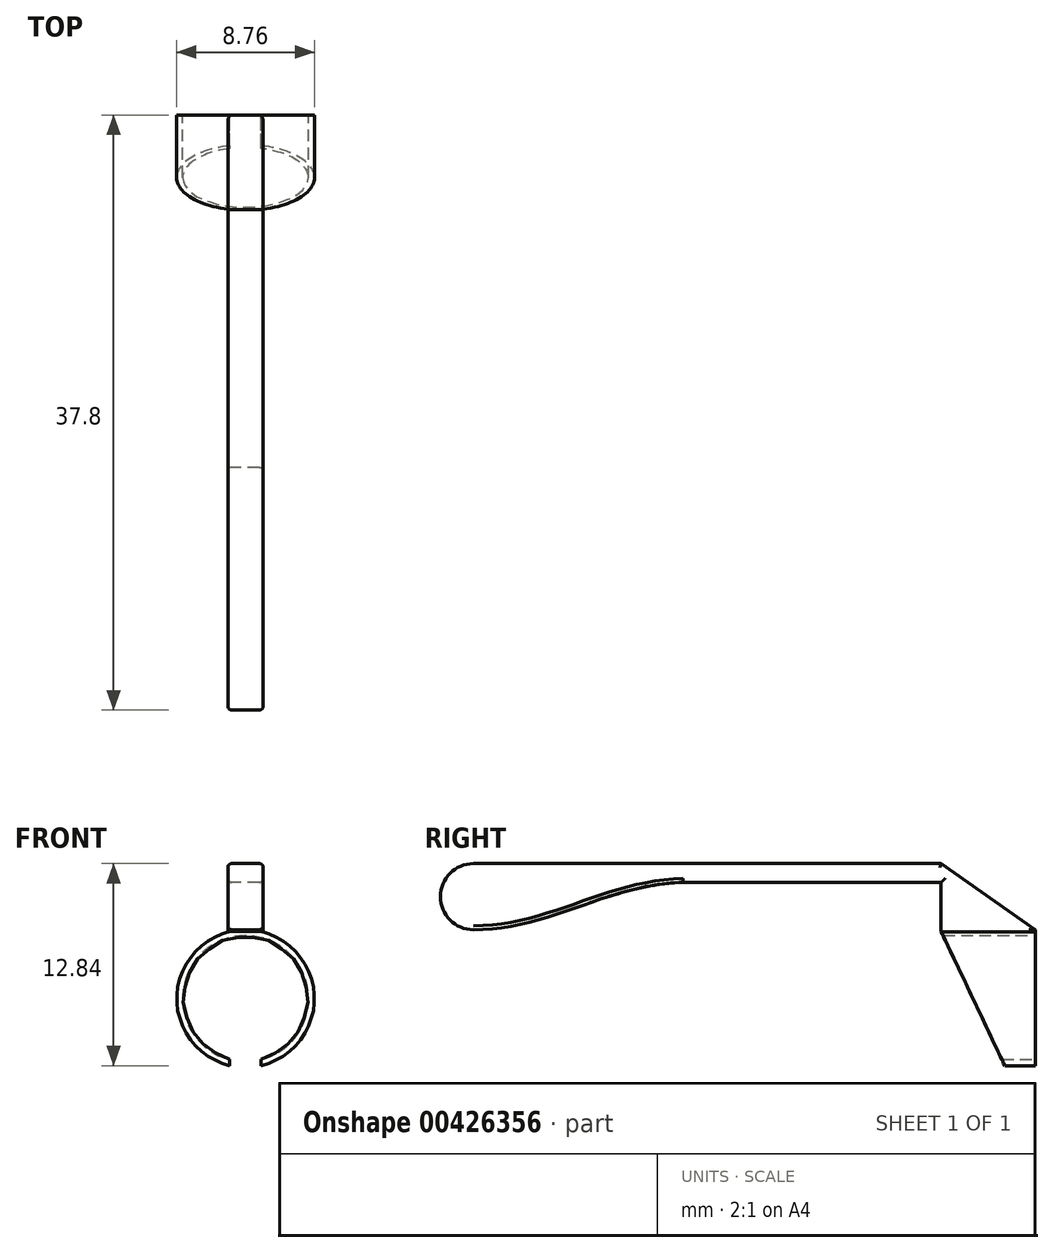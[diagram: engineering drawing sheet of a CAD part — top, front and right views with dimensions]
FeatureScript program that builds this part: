
annotation { "Feature Type Name" : "Feature", "Feature Type Description" : "" }
export const myFeature = defineFeature(function(context is Context, id is Id, definition is map)
    precondition{}
    {
        {
            var Q0;
            Q0=qCreatedBy(makeId("Front.planeOp"),FACE);
            var sketch = newSketch(context, id + "F0", { "sketchPlane" : qUnion([Q0])});
            skCircle(sketch, "E0", {"center": v(0, 0) * mm, "radius": 4.38 * mm});
            skCircle(sketch, "E1", {"center": v(0, 0) * mm, "radius": 4 * mm});
            skSolve(sketch);
        }
        {
            var Q0;
            Q0 = qSketchRegion(id + "F0", true);
            extrude(context, id + "F1", {"entities" : qUnion([Q0]), "depth" : 6 * mm});
        }
        {
            var Q0;
            Q0=qCreatedBy(makeId("Right.planeOp"),FACE);
            var sketch = newSketch(context, id + "F2", { "sketchPlane" : qUnion([Q0])});
            skLineSegment(sketch, "E2", {"start": v(0, 0) * mm, "end": v(0, 4.38) * mm});
            skLineSegment(sketch, "E3", {"start": v(0, 4.37) * mm, "end": v(-6, 8.57) * mm});
            skLineSegment(sketch, "E4", {"start": v(-26.02, 4.37) * mm, "end": v(-25.98, 4.7) * mm});
            skLineSegment(sketch, "E5", {"start": v(-22.4, 7.37) * mm, "end": v(-6, 7.37) * mm});
            skLineSegment(sketch, "E6", {"start": v(-6, 7.38) * mm, "end": v(-6, 4.37) * mm});
            skLineSegment(sketch, "E7", {"start": v(-6, 4.38) * mm, "end": v(0, 4.38) * mm});
            skLineSegment(sketch, "E8", {"start": v(-6, 8.57) * mm, "end": v(-35.7, 8.57) * mm});
            skArc(sketch, "E9", {"start": v(-35.7, 8.57) * mm, "mid": v(-37.8, 6.47) * mm, "end": v(-35.7, 4.37) * mm});
            skFitSpline(sketch, "E10", {"points": [v(-35.7, 4.37) * mm, v(-22.4, 7.37) * mm], "startDerivative": vector(14.58, 0) * mm, "endDerivative": vector(14.36, 0.28) * mm});
            skSolve(sketch);
        }
        {
            var Q0;
            Q0 = qSketchRegion(id + "F2", true);
            extrude(context, id + "F3", {"entities" : qUnion([Q0]), "operationType" : NewBodyOperationType.ADD, "depth" : 2.25 * mm, "symmetric" : true});
        }
        {
            var Q0;
            Q0=makeQuery(id+"F3.opExtrude","CAP_EDGE",EDGE,{"disambiguationData":[OSD([sQuery(id+"F2.wireOp",EDGE,"E8")])],"isStart":false});
            var Q1;
            Q1=makeQuery(id+"F3.opExtrude","CAP_EDGE",EDGE,{"disambiguationData":[OSD([sQuery(id+"F2.wireOp",EDGE,"E3")])],"isStart":false});
            var Q2;
            Q2=makeQuery(id+"F3.opExtrude","CAP_EDGE",EDGE,{"disambiguationData":[OSD([sQuery(id+"F2.wireOp",EDGE,"E3")])],"isStart":true});
            var Q3;
            Q3=makeQuery(id+"F3.opExtrude","CAP_EDGE",EDGE,{"disambiguationData":[OSD([sQuery(id+"F2.wireOp",EDGE,"E8")])],"isStart":true});
            var Q4;
            Q4=makeQuery(id+"F3.opExtrude","CAP_EDGE",EDGE,{"disambiguationData":[OSD([sQuery(id+"F2.wireOp",EDGE,"E5")])],"isStart":true});
            var Q5;
            Q5=makeQuery(id+"F3.opExtrude","CAP_EDGE",EDGE,{"disambiguationData":[OSD([sQuery(id+"F2.wireOp",EDGE,"E5")])],"isStart":false});
            var Q6;
            Q6=makeQuery(id+"F3.opExtrude","CAP_EDGE",EDGE,{"disambiguationData":[OSD([sQuery(id+"F2.wireOp",EDGE,"E6")])],"isStart":true});
            var Q7;
            Q7=makeQuery(id+"F3.opExtrude","CAP_EDGE",EDGE,{"disambiguationData":[OSD([sQuery(id+"F2.wireOp",EDGE,"E6")])],"isStart":false});
            fillet(context, id + "F4", {"entities" : qUnion([Q0, Q1, Q2, Q3, Q4, Q5, Q6, Q7]), "radius" : .25 * mm, "tangentPropagation" : true, "allowEdgeOverflow" : false});
        }
        {
            var Q0;
            Q0=makeQuery(id+"F3.opExtrude","SWEPT_FACE",FACE,{"disambiguationData":[OSD([sQuery(id+"F2.wireOp",EDGE,"E7")])]});
            extrude(context, id + "F5", {"entities" : qUnion([Q0]), "operationType" : NewBodyOperationType.ADD, "depth" : .2 * mm});
        }
        {
            var Q0;
            Q0=qCreatedBy(makeId("Right.planeOp"),FACE);
            var sketch = newSketch(context, id + "F6", { "sketchPlane" : qUnion([Q0])});
            skLineSegment(sketch, "E11", {"start": v(-1.9, -4.38) * mm, "end": v(-6, 4.26) * mm});
            skLineSegment(sketch, "E12", {"start": v(-6, 4.26) * mm, "end": v(-6.6, 4.26) * mm});
            skLineSegment(sketch, "E13", {"start": v(-6.6, 4.26) * mm, "end": v(-6.6, -4.94) * mm});
            skLineSegment(sketch, "E14", {"start": v(-6.6, -4.94) * mm, "end": v(-1.9, -4.94) * mm});
            skLineSegment(sketch, "E15", {"start": v(-1.9, -4.94) * mm, "end": v(-1.9, -4.38) * mm});
            skSolve(sketch);
        }
        {
            var Q0;
            Q0 = qSketchRegion(id + "F6", true);
            extrude(context, id + "F7", {"entities" : qUnion([Q0]), "operationType" : NewBodyOperationType.REMOVE, "oppositeDirection" : true, "depth" : 25 * mm, "symmetric" : true});
        }
        {
            var Q0;
            Q0=qCreatedBy(makeId("Front.planeOp"),FACE);
            var sketch = newSketch(context, id + "F8", { "sketchPlane" : qUnion([Q0])});
            skLineSegment(sketch, "E16.bottom", {"start": v(-1, -5) * mm, "end": v(1, -5) * mm});
            skLineSegment(sketch, "E16.top", {"start": v(-1, -2) * mm, "end": v(1, -2) * mm});
            skLineSegment(sketch, "E16.left", {"start": v(-1, -5) * mm, "end": v(-1, -2) * mm});
            skLineSegment(sketch, "E16.right", {"start": v(1, -5) * mm, "end": v(1, -2) * mm});
            skPoint(sketch, "E16.middle", {"position": v(0, -3.5) * mm});
            skSolve(sketch);
        }
        {
            var Q0;
            Q0 = qSketchRegion(id + "F8", true);
            extrude(context, id + "F9", {"entities" : qUnion([Q0]), "operationType" : NewBodyOperationType.REMOVE, "endBound" : BoundingType.THROUGH_ALL, "depth" : 25 * mm});
        }
    });
